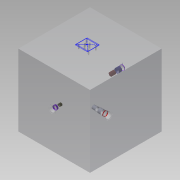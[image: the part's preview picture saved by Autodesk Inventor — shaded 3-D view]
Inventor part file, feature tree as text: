
AUTODESK INVENTOR PART (.ipt)
format: ipt  version: 2014 (Build 180170000, 170)  size: 389,120 bytes
history: native  units: mm
features: other x69, sketch x16, extrude x1
ambient origin geometry x8: Origin, YZ Plane, XZ Plane, XY Plane, X Axis, Y Axis, Z Axis, Center Point
bodies: 实体1 (feature_tree)
feature tree (86):
  other  "NET12"
  other  "NET8"
  other  "NULLNET"
  other  "NET1"
  other  "NET11"
  other  "NET7"
  extrude  "拉伸1"  TaperAngle=0.0deg  [1 undecoded]
  other  "UCS1"
  other  "UCS2"
  other  "UCS3"
  other  "UCS4"
  other  "UCS5"
  other  "UCS6"
  other  "Footprint1"
  sketch  "草图1"  dims[d0=300.0mm d1=0.0mm]
  sketch  "草图5"  dims[d14=0.0mm d15=0.0mm d16=0.0mm d17=0.0mm d18=0.0mm d19=0.0mm]
  other  "曲面1"
  sketch  "草图6"  dims[d20=0.0mm d21=0.0mm d22=0.0mm d23=0.0mm d24=0.0mm d25=0.0mm]
  other  "曲面2"
  sketch  "草图7"  dims[d26=0.0mm d27=0.0mm d28=0.0mm d29=0.0mm d30=0.0mm d31=0.0mm]
  other  "曲面3"
  sketch  "草图9"  dims[d52=0.0mm]
  other  "曲面4"
  sketch  "草图10"  dims[d56=-30.09mm]
  other  "曲面5"
  sketch  "草图11"  dims[d57=0.13mm d58=0.0mm]
  other  "曲面6"
  sketch  "草图12"  dims[d59=0.13mm d60=-10.307443mm]
  other  "曲面7"
  sketch  "草图14"  dims[d62=6.35mm d63=0.0mm]
  other  "曲面8"
  sketch  "草图15"  dims[d64=0.0mm]
  other  "曲面9"
  sketch  "草图16"  dims[d68=-48.42mm]
  other  "曲面10"
  sketch  "草图17"  dims[d69=0.13mm d70=0.0mm d71=0.13mm d72=-10.307443mm d73=-31.75mm d74=13.5mm d75=0.0mm d76=-15.07mm d77=3.18mm d78=0.0mm d79=0.0mm d83=-48.42mm d84=0.13mm d85=0.0mm d86=0.13mm d87=-10.307443mm d88=-31.75mm d89=13.5mm d90=0.0mm d91=-15.07mm d92=3.18mm d93=0.0mm]
  other  "曲面11"
  other  "10-1cone"
  other  "3-1cone"
  other  "9-1cone"
  other  "UCS1: YZ 平面"
  other  "UCS1: XZ 平面"
  other  "UCS1: XY 平面"
  other  "UCS1: X 轴"
  other  "UCS1: Y 轴"
  other  "UCS1: Z 轴"
  other  "UCS1: 原点"
  other  "UCS2: YZ 平面"
  other  "UCS2: XZ 平面"
  other  "UCS2: XY 平面"
  other  "UCS2: X 轴"
  other  "UCS2: Y 轴"
  other  "UCS2: Z 轴"
  other  "UCS2: 原点"
  other  "UCS3: YZ 平面"
  other  "UCS3: XZ 平面"
  other  "UCS3: XY 平面"
  other  "UCS3: X 轴"
  other  "UCS3: Y 轴"
  other  "UCS3: Z 轴"
  other  "UCS3: 原点"
  other  "UCS4: YZ 平面"
  other  "UCS4: XZ 平面"
  other  "UCS4: XY 平面"
  other  "UCS4: X 轴"
  other  "UCS4: Y 轴"
  other  "UCS4: Z 轴"
  other  "UCS4: 原点"
  other  "UCS5: YZ 平面"
  other  "UCS5: XZ 平面"
  other  "UCS5: XY 平面"
  other  "UCS5: X 轴"
  other  "UCS5: Y 轴"
  other  "UCS5: Z 轴"
  other  "UCS5: 原点"
  other  "UCS6: YZ 平面"
  other  "UCS6: XZ 平面"
  other  "UCS6: XY 平面"
  other  "UCS6: X 轴"
  other  "UCS6: Y 轴"
  other  "UCS6: Z 轴"
  other  "UCS6: 原点"
  sketch  "草图2"  dims[d2=0.0mm d3=0.0mm d4=0.0mm d5=0.0mm d6=0.0mm d7=0.0mm]
  sketch  "草图4"  dims[d8=0.0mm d9=0.0mm d10=0.0mm d11=0.0mm d12=0.0mm d13=0.0mm]
  sketch  "草图8"  dims[d32=0.0mm d33=0.0mm d34=0.0mm d35=0.0mm d36=0.0mm d37=0.0mm d38=0.0mm]
  sketch  "草图13"  dims[d61=-15.07mm]
note: 1 required parameter value undecoded (feature->parameter linkage not recoverable at this tier; creation-order binding heuristic only, values carry confidence <= 0.55)
